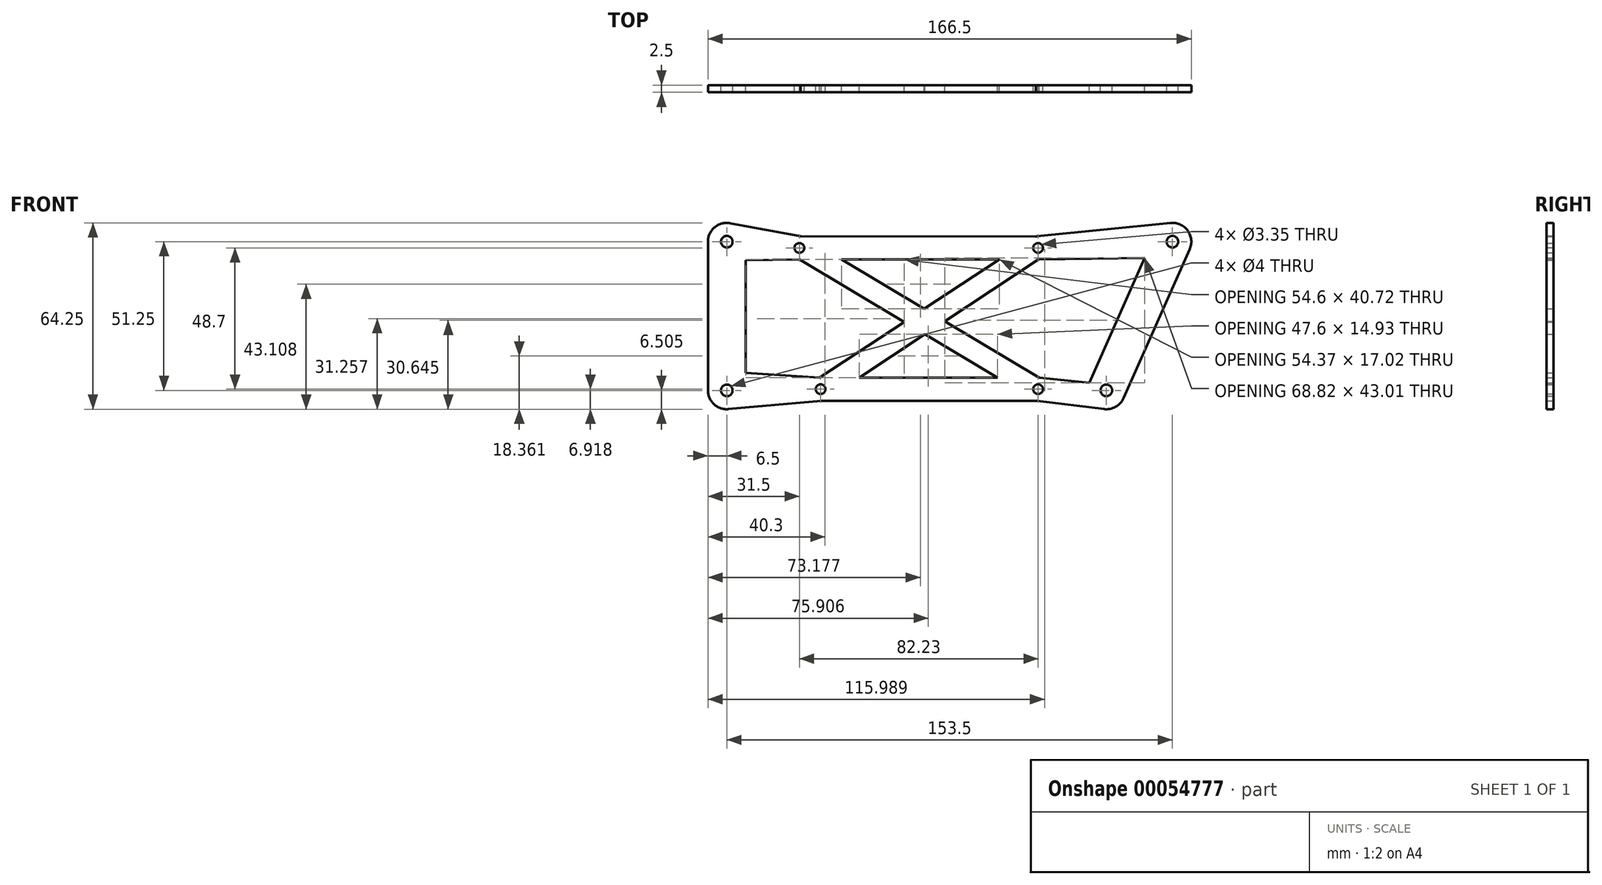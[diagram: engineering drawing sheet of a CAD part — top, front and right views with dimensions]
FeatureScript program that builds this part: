
annotation { "Feature Type Name" : "Feature", "Feature Type Description" : "" }
export const myFeature = defineFeature(function(context is Context, id is Id, definition is map)
    precondition{}
    {
        {
            var Q0;
            Q0=qCreatedBy(makeId("Front.planeOp"),FACE);
            var sketch = newSketch(context, id + "F0", { "sketchPlane" : qUnion([Q0])});
            skCircle(sketch, "E0", {"center": v(0, -25.63) * mm, "radius": 2 * mm});
            skCircle(sketch, "E1", {"center": v(0, 25.63) * mm, "radius": 2 * mm});
            skCircle(sketch, "E2", {"center": v(153.5, 25.63) * mm, "radius": 2 * mm});
            skCircle(sketch, "E3", {"center": v(130.75, -25.62) * mm, "radius": 2 * mm});
            skCircle(sketch, "E4", {"center": v(107.23, 23.49) * mm, "radius": 1.68 * mm});
            skCircle(sketch, "E5", {"center": v(25, 23.49) * mm, "radius": 1.67 * mm});
            skCircle(sketch, "E6", {"center": v(32.32, -25.21) * mm, "radius": 1.68 * mm});
            skCircle(sketch, "E7", {"center": v(107.23, -25.21) * mm, "radius": 1.68 * mm});
            skArc(sketch, "E8", {"start": v(1.2, 32.01) * mm, "mid": v(-4.15, 30.63) * mm, "end": v(-6.5, 25.63) * mm});
            skArc(sketch, "E9", {"start": v(-6.5, -25.63) * mm, "mid": v(-4.38, -30.42) * mm, "end": v(0.59, -32.1) * mm});
            skArc(sketch, "E10", {"start": v(129.95, -32.08) * mm, "mid": v(133.95, -31.28) * mm, "end": v(136.7, -28.26) * mm});
            skArc(sketch, "E11", {"start": v(159.44, 22.99) * mm, "mid": v(158.77, 29.44) * mm, "end": v(152.85, 32.1) * mm});
            skLineSegment(sketch, "E12", {"start": v(0.59, -32.1) * mm, "end": v(32.5, -29.21) * mm});
            skLineSegment(sketch, "E13", {"start": v(-6.5, -25.63) * mm, "end": v(-6.5, 25.63) * mm});
            skLineSegment(sketch, "E14", {"start": v(1.2, 32.01) * mm, "end": v(25.37, 27.49) * mm});
            skLineSegment(sketch, "E15", {"start": v(25.37, 27.49) * mm, "end": v(106.5, 27.42) * mm});
            skLineSegment(sketch, "E16", {"start": v(106.83, 27.47) * mm, "end": v(152.85, 32.1) * mm});
            skLineSegment(sketch, "E17", {"start": v(159.44, 22.99) * mm, "end": v(136.7, -28.26) * mm});
            skLineSegment(sketch, "E18", {"start": v(129.95, -32.08) * mm, "end": v(106.98, -29.21) * mm});
            skLineSegment(sketch, "E19", {"start": v(106.98, -29.21) * mm, "end": v(32.5, -29.21) * mm});
            skLineSegment(sketch, "E20", {"start": v(6.5, -19.54) * mm, "end": v(6.5, 19.22) * mm});
            skLineSegment(sketch, "E21", {"start": v(39.5, 19.49) * mm, "end": v(93.86, 19.49) * mm});
            skLineSegment(sketch, "E22", {"start": v(107.29, 19.49) * mm, "end": v(143.9, 20.02) * mm});
            skLineSegment(sketch, "E23", {"start": v(143.9, 20.02) * mm, "end": v(124.8, -22.99) * mm});
            skLineSegment(sketch, "E24", {"start": v(124.8, -22.99) * mm, "end": v(107.64, -21.23) * mm});
            skLineSegment(sketch, "E25", {"start": v(31.91, -21.23) * mm, "end": v(6.5, -19.54) * mm});
            skLineSegment(sketch, "E26", {"start": v(31.91, -21.23) * mm, "end": v(61.1, -2.05) * mm});
            skLineSegment(sketch, "E27", {"start": v(107.29, 19.49) * mm, "end": v(75.08, -1.78) * mm});
            skLineSegment(sketch, "E28", {"start": v(25.06, 19.49) * mm, "end": v(61.1, -2.05) * mm});
            skLineSegment(sketch, "E29", {"start": v(107.64, -21.23) * mm, "end": v(75.08, -1.78) * mm});
            skLineSegment(sketch, "E30.trimOffspring", {"start": v(67.97, 2.47) * mm, "end": v(39.5, 19.49) * mm});
            skLineSegment(sketch, "E31.trimOffspring", {"start": v(67.97, 2.47) * mm, "end": v(93.86, 19.49) * mm});
            skLineSegment(sketch, "E32.trimOffspring", {"start": v(68.22, -6.3) * mm, "end": v(93.2, -21.23) * mm});
            skLineSegment(sketch, "E33.trimOffspring", {"start": v(68.22, -6.3) * mm, "end": v(45.6, -21.23) * mm});
            skArc(sketch, "E34.trimOffspring", {"start": v(106.83, 27.47) * mm, "mid": v(106.66, 27.45) * mm, "end": v(106.5, 27.42) * mm});
            skLineSegment(sketch, "E35.trimOffspring", {"start": v(93.2, -21.23) * mm, "end": v(45.6, -21.23) * mm});
            skPoint(sketch, "E36.orphan", {"position": v(0, -19.11) * mm});
            skLineSegment(sketch, "E37.trimOffspring", {"start": v(6.5, 19.22) * mm, "end": v(25.06, 19.49) * mm});
            skPoint(sketch, "E38.trimOffspring.start.orphan", {"position": v(0, 19.13) * mm});
            skPoint(sketch, "E39.orphan", {"position": v(25.74, 27.42) * mm});
            skSolve(sketch);
        }
        {
            var Q0;
            Q0=makeQuery(id+"F0.imprint","IMPRINT",FACE,{"disambiguationData":[TD([[makeQuery(id+"F0.imprint","IMPRINT",EDGE,{"derivedFrom":sQuery(id+"F0.wireOp",EDGE,"E0")}),-1.0]])]});
            extrude(context, id + "F1", {"entities" : qUnion([Q0]), "depth" : 2.5 * mm});
        }
    });
